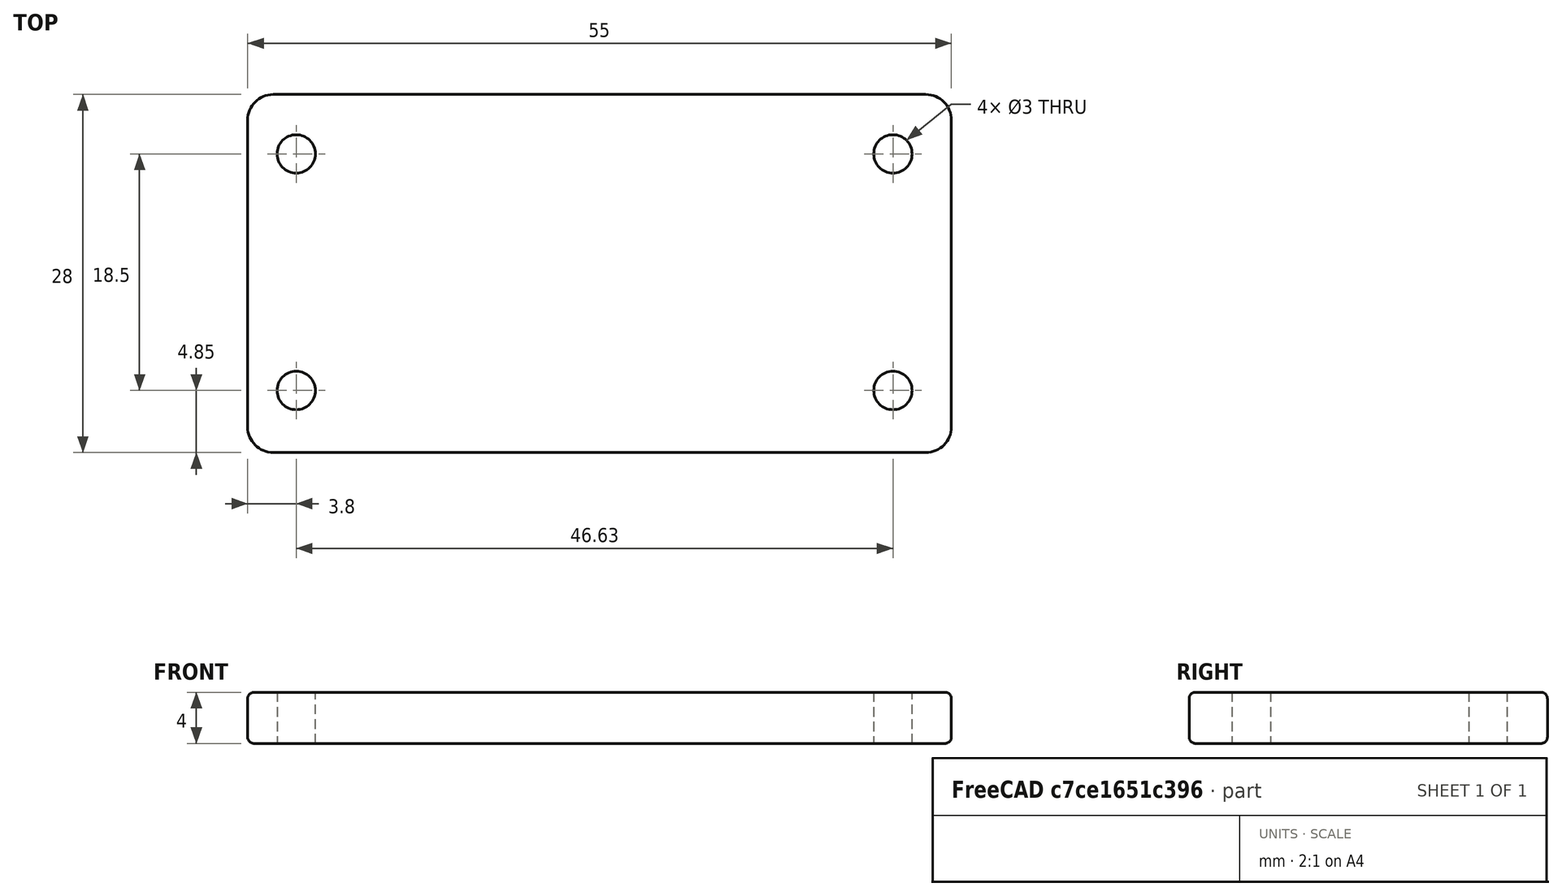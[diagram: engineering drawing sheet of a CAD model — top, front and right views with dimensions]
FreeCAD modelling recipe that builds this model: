
FCSTD DOCUMENT  (FreeCAD 0.21R33668 +7 (Git))
Label: nrf52_Base_July_10_2024
License: All rights reserved
LicenseURL: https://en.wikipedia.org/wiki/All_rights_reserved
objects: Part::Cylinder×4, Mesh::Feature×1, Part::Box×1, Part::MultiFuse×1, Part::Cut×1, Part::Fillet×1
note: 8 computed .brp shape members not serialized (recipe doc carries the construction recipe); baked Part::Feature solids carry a one-line shape summary decoded from their .brp

FEATURE [Mesh::Feature] Adafruit_Feather_nRF52840
  Placement = pos=(0,0,0) rot=(1,0,0;4.71239rad)
FEATURE [Part::Box] Box  label="Plate"
  AttacherType = Attacher::AttachEngine3D
  Height = 4
  Length = 55
  Placement = pos=(-81,-8.5,-52.5) rot=(0,0,1;0rad)
  Width = 28
FEATURE [Part::Cylinder] Cylinder
  Angle = 360
  AttacherType = Attacher::AttachEngine3D
  FirstAngle = 0
  Height = 10
  Placement = pos=(-77.2,-3.65,0) rot=(0,0,1;0rad)
  Radius = 1.5
  SecondAngle = 0
FEATURE [Part::Cylinder] Cylinder001
  Angle = 360
  AttacherType = Attacher::AttachEngine3D
  FirstAngle = 0
  Height = 10
  Placement = pos=(-77.2,14.85,0) rot=(0,0,1;0rad)
  Radius = 1.5
  SecondAngle = 0
FEATURE [Part::Cylinder] Cylinder002
  Angle = 360
  AttacherType = Attacher::AttachEngine3D
  FirstAngle = 0
  Height = 10
  Placement = pos=(-30.57,-3.65,0) rot=(0,0,1;0rad)
  Radius = 1.5
  SecondAngle = 0
FEATURE [Part::Cylinder] Cylinder003
  Angle = 360
  AttacherType = Attacher::AttachEngine3D
  FirstAngle = 0
  Height = 10
  Placement = pos=(-30.57,14.85,0) rot=(0,0,1;0rad)
  Radius = 1.5
  SecondAngle = 0
FEATURE [Part::MultiFuse] Fusion  label="Holes"
  Placement = pos=(0,0,-56) rot=(0,0,1;0rad)
  Shapes = -> [Cylinder,Cylinder001,Cylinder002,Cylinder003]
FEATURE [Part::Cut] Cut  label="Plt"
  Base = -> Box
  Tool = -> Fusion
FEATURE [Part::Fillet] Fillet  label="BasePlate"
  Base = -> Cut
  Edges = 12 edges: [Edge1 r=2,Edge2 r=0.5,Edge3 r=2,Edge4 r=0.5,Edge5 r=0.5,Edge6 r=2,Edge7 r=0.5,Edge8 r=0.5,Edge9 r=0.5,Edge14 r=0.5,Edge15 r=2,Edge16 r=0.5]
